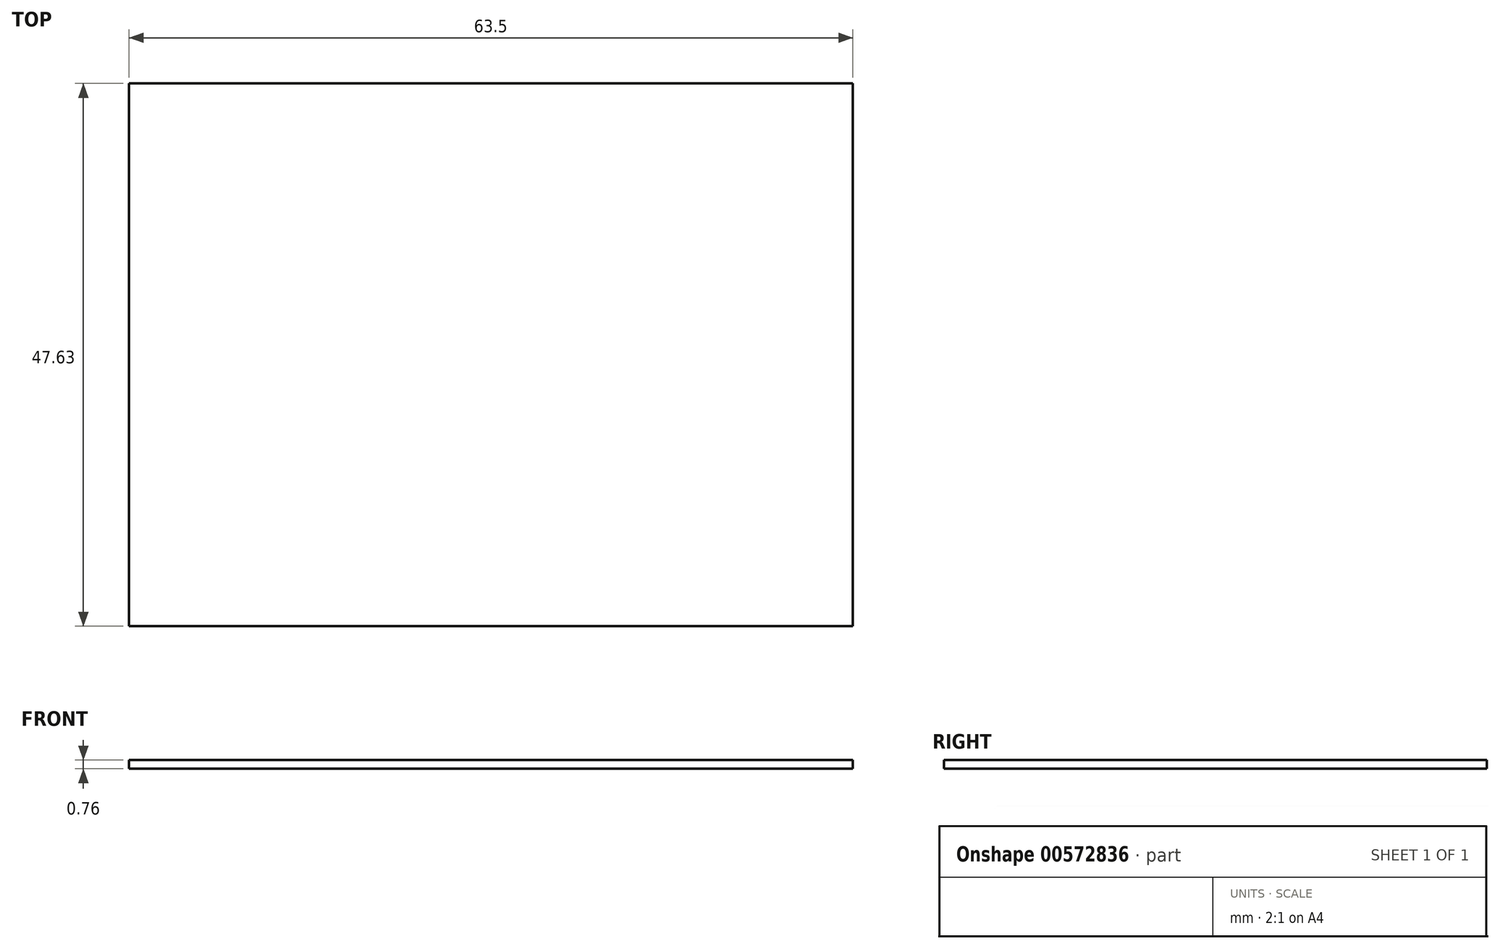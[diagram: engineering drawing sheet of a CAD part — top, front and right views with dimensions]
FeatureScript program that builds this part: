
annotation { "Feature Type Name" : "Feature", "Feature Type Description" : "" }
export const myFeature = defineFeature(function(context is Context, id is Id, definition is map)
    precondition{}
    {
        {
            var Q0;
            Q0=qCreatedBy(makeId("Top.planeOp"),FACE);
            var sketch = newSketch(context, id + "F0", { "sketchPlane" : qUnion([Q0])});
            skLineSegment(sketch, "E0.bottom", {"start": v(6.82, 27.7) * mm, "end": v(70.32, 27.7) * mm});
            skLineSegment(sketch, "E0.top", {"start": v(6.82, -19.92) * mm, "end": v(70.32, -19.92) * mm});
            skLineSegment(sketch, "E0.left", {"start": v(6.82, 27.7) * mm, "end": v(6.82, -19.92) * mm});
            skLineSegment(sketch, "E0.right", {"start": v(70.32, 27.7) * mm, "end": v(70.32, -19.92) * mm});
            skSolve(sketch);
        }
        {
            var Q0;
            Q0 = qSketchRegion(id + "F0", true);
            extrude(context, id + "F1", {"entities" : qUnion([Q0]), "depth" : 0.76 * mm, "offsetDistance" : 25.4 * mm});
        }
        {
            var Q0;
            Q0=makeQuery(id+"F1.opExtrude","SWEPT_BODY",BODY,{"disambiguationData":[OSD([sQuery(id+"F0.wireOp",EDGE,"E0.bottom"),sQuery(id+"F0.wireOp",EDGE,"E0.top"),sQuery(id+"F0.wireOp",EDGE,"E0.left"),sQuery(id+"F0.wireOp",EDGE,"E0.right")])]});
            var Q1;
            Q1=makeQuery(id+"F1.opExtrude","CAP_VERTEX",VERTEX,{"disambiguationData":[OSD([sQuery(id+"F0.wireOp",EDGE,"E0.top"),sQuery(id+"F0.wireOp",EDGE,"E0.left")])],"isStart":false});
            var Q2;
            Q2=qCreatedBy(makeId("Origin.pointOp"),VERTEX);
            transform(context, id + "F2", {"entities" : qUnion([Q0]), "transformType" : TransformType.TRANSLATION_ENTITY, "oppositeDirectionEntity" : false, "transformLine" : qUnion([Q1, Q2]), "makeCopy" : false});
        }
        {
            var Q0;
            Q0=makeQuery(id+"F1.opExtrude","SWEPT_BODY",BODY,{"disambiguationData":[OSD([sQuery(id+"F0.wireOp",EDGE,"E0.bottom"),sQuery(id+"F0.wireOp",EDGE,"E0.top"),sQuery(id+"F0.wireOp",EDGE,"E0.left"),sQuery(id+"F0.wireOp",EDGE,"E0.right")])]});
            var Q1;
            Q1=qCreatedBy(makeId("Front.planeOp"),FACE);
            transform(context, id + "F3", {"entities" : qUnion([Q0]), "transformType" : TransformType.TRANSLATION_DISTANCE, "transformDirection" : qUnion([Q1]), "distance" : 24.64 * mm, "makeCopy" : false});
        }
    });
